# Revit family: 201_KNT-_
name_source: partatom
category: Air Terminals
units: mm (PartAtom-declared; Revit-internal decimal feet)

## family parameters
Always vertical = Yes
Cut with Voids When Loaded = No
Part Type = Normal
Room Calculation Point = Yes
Round Connector Dimension = Use Diameter
Shared = No
Work Plane-Based = No

## types (3) — shared parameters
CAT0 = Yes
CL_Location_5000 = 5000 mm  [stored 16.4042 ft]
Description = AIR SUPPLY VALVE WITH MOUNTING FRAME
FL = 15 mm  [stored 0.0492126 ft]
L_ARR = 400 mm  [stored 1.31234 ft]
Manufacturer = Alnor
QmdConnectorList = 201;D
URL = http://www.ventilation-alnor.co.uk
W_ARR = 400 mm  [stored 1.31234 ft]
XRefLineVPlnId = 7453
YRefLineVPlnId = 7456
magiPartTypeId = 201
magiProductFamilyId = KNT-*
zero-valued in all types: CLBTZ, H_ARR

## per-type parameters (varying)
| type | D | DO | DO1 |
| KNT-100 | 100 mm | 135 mm  [stored 0.442913 ft] | 128 mm |
| KNT-160 | 160 mm | 205 mm | 195 mm |
| KNT-125 | 125 mm | 165 mm | 157 mm |

note: column(s) folded — value = type name in every type: MC Product Code, magiProductId

note: [stored X ft] marks values corroborated as IEEE doubles in the binary element streams (Revit-internal decimal feet)

## geometry (parser evidence)
native form markers: Blend x2, Sweep x3
no freeform markers — native parametric forms only
